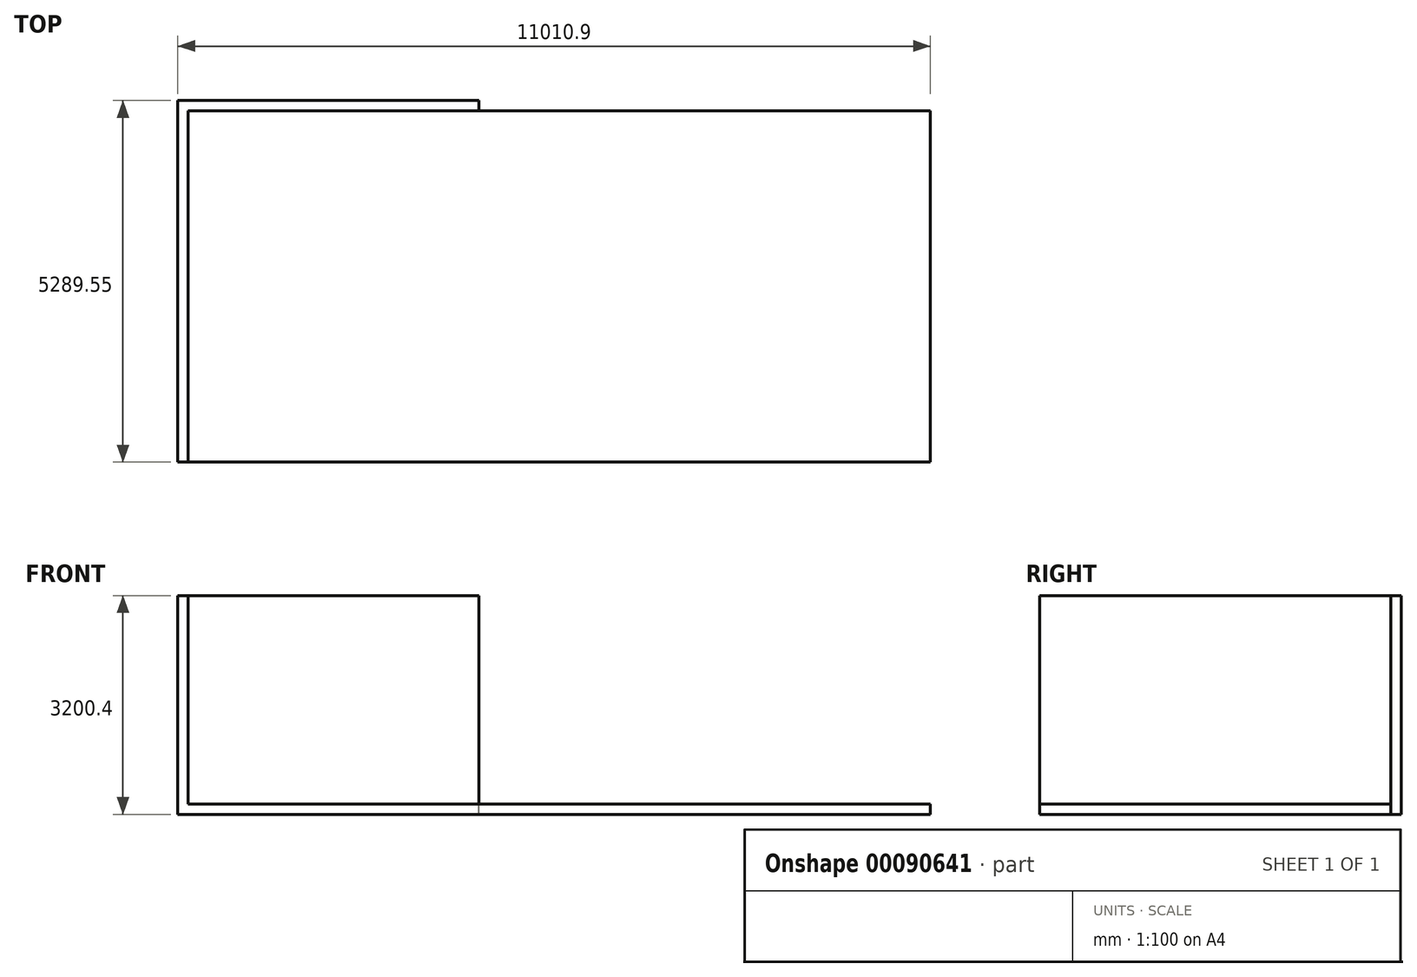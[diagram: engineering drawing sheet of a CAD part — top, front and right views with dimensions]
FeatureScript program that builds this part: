
annotation { "Feature Type Name" : "Feature", "Feature Type Description" : "" }
export const myFeature = defineFeature(function(context is Context, id is Id, definition is map)
    precondition{}
    {
        {
            var Q0;
            Q0=qCreatedBy(makeId("Top.planeOp"),FACE);
            var sketch = newSketch(context, id + "F0", { "sketchPlane" : qUnion([Q0])});
            skLineSegment(sketch, "E0.bottom", {"start": v(0, 0) * mm, "end": v(10858.5, 0) * mm});
            skLineSegment(sketch, "E0.top", {"start": v(0, 5137.15) * mm, "end": v(10858.5, 5137.15) * mm});
            skLineSegment(sketch, "E0.left", {"start": v(0, 0) * mm, "end": v(0, 5137.15) * mm});
            skLineSegment(sketch, "E0.right", {"start": v(10858.5, 0) * mm, "end": v(10858.5, 5137.15) * mm});
            skLineSegment(sketch, "E1.bottom", {"start": v(0, 0) * mm, "end": v(-152.4, 0) * mm});
            skLineSegment(sketch, "E1.top", {"start": v(0, 5137.15) * mm, "end": v(-152.4, 5137.15) * mm});
            skLineSegment(sketch, "E1.right", {"start": v(-152.4, 0) * mm, "end": v(-152.4, 5137.15) * mm});
            skLineSegment(sketch, "E2.bottom", {"start": v(-152.4, 0) * mm, "end": v(4254.5, 0) * mm});
            skLineSegment(sketch, "E2.top", {"start": v(-152.4, -152.4) * mm, "end": v(4254.5, -152.4) * mm});
            skLineSegment(sketch, "E2.left", {"start": v(-152.4, 0) * mm, "end": v(-152.4, -152.4) * mm});
            skLineSegment(sketch, "E2.right", {"start": v(4254.5, 0) * mm, "end": v(4254.5, -152.4) * mm});
            skLineSegment(sketch, "E3.bottom", {"start": v(-152.4, 5137.15) * mm, "end": v(4254.5, 5137.15) * mm});
            skLineSegment(sketch, "E3.top", {"start": v(-152.4, 5289.55) * mm, "end": v(4254.5, 5289.55) * mm});
            skLineSegment(sketch, "E3.left", {"start": v(-152.4, 5137.15) * mm, "end": v(-152.4, 5289.55) * mm});
            skLineSegment(sketch, "E3.right", {"start": v(4254.5, 5137.15) * mm, "end": v(4254.5, 5289.55) * mm});
            skLineSegment(sketch, "E4.bottom", {"start": v(4254.5, 0) * mm, "end": v(10858.5, 0) * mm});
            skLineSegment(sketch, "E4.top", {"start": v(4254.5, -1828.8) * mm, "end": v(10858.5, -1828.8) * mm});
            skLineSegment(sketch, "E4.left", {"start": v(4254.5, 0) * mm, "end": v(4254.5, -1828.8) * mm});
            skLineSegment(sketch, "E4.right", {"start": v(10858.5, 0) * mm, "end": v(10858.5, -1828.8) * mm});
            skLineSegment(sketch, "E5.bottom", {"start": v(4254.5, 5137.15) * mm, "end": v(10858.5, 5137.15) * mm});
            skLineSegment(sketch, "E5.top", {"start": v(4254.5, 6965.95) * mm, "end": v(10858.5, 6965.95) * mm});
            skLineSegment(sketch, "E5.left", {"start": v(4254.5, 5137.15) * mm, "end": v(4254.5, 6965.95) * mm});
            skLineSegment(sketch, "E5.right", {"start": v(10858.5, 5137.15) * mm, "end": v(10858.5, 6965.95) * mm});
            skSolve(sketch);
        }
        {
            var Q0;
            Q0=makeQuery(id+"F0.imprint","IMPRINT",FACE,{"disambiguationData":[TD([[makeQuery(id+"F0.imprint","IMPRINT",EDGE,{"derivedFrom":sQuery(id+"F0.wireOp",EDGE,"E3.top")}),-1.0]])]});
            var Q1;
            {var subQ0=sQuery(id+"F0.wireOp",EDGE,"E0.left");Q1=makeQuery(id+"F0.imprint","IMPRINT",FACE,{"disambiguationData":[TD([[makeQuery(id+"F0.imprint","IMPRINT",EDGE,{"derivedFrom":subQ0}),1.0]])]});}
            extrude(context, id + "F1", {"entities" : qUnion([Q0, Q1]), "depth" : 3048 * mm});
        }
        {
            var Q0;
            {var subQ2=sQuery(id+"F0.wireOp",EDGE,"E0.bottom");Q0=makeQuery(id+"F0.imprint","IMPRINT",FACE,{"disambiguationData":[TD([[makeQuery(id+"F0.imprint","IMPRINT",EDGE,{"derivedFrom":subQ2}),1.0]])]});}
            var Q1;
            {var subQ0=sQuery(id+"F0.wireOp",EDGE,"E0.left");Q1=makeQuery(id+"F0.imprint","IMPRINT",FACE,{"disambiguationData":[TD([[makeQuery(id+"F0.imprint","IMPRINT",EDGE,{"derivedFrom":subQ0}),1.0]])]});}
            var Q2;
            Q2=makeQuery(id+"F0.imprint","IMPRINT",FACE,{"disambiguationData":[TD([[makeQuery(id+"F0.imprint","IMPRINT",EDGE,{"derivedFrom":sQuery(id+"F0.wireOp",EDGE,"E3.top")}),-1.0]])]});
            var Q3;
            Q3=makeQuery(id+"F0.imprint","IMPRINT",FACE,{"disambiguationData":[TD([[makeQuery(id+"F0.imprint","IMPRINT",EDGE,{"derivedFrom":sQuery(id+"F0.wireOp",EDGE,"E0.right")}),1.0]])]});
            var Q4;
            {var subQ3=sQuery(id+"F0.wireOp",EDGE,"E4.bottom");Q4=makeQuery(id+"F0.imprint","IMPRINT",FACE,{"disambiguationData":[TD([[makeQuery(id+"F0.imprint","IMPRINT",EDGE,{"derivedFrom":subQ3}),-1.0]])]});}
            var Q5;
            {var subQ3=sQuery(id+"F0.wireOp",EDGE,"E5.bottom");Q5=makeQuery(id+"F0.imprint","IMPRINT",FACE,{"disambiguationData":[TD([[makeQuery(id+"F0.imprint","IMPRINT",EDGE,{"derivedFrom":subQ3}),1.0]])]});}
            extrude(context, id + "F2", {"entities" : qUnion([Q0, Q1, Q2, Q3, Q4, Q5]), "operationType" : NewBodyOperationType.ADD, "oppositeDirection" : true, "depth" : 152.4 * mm});
        }
    });
